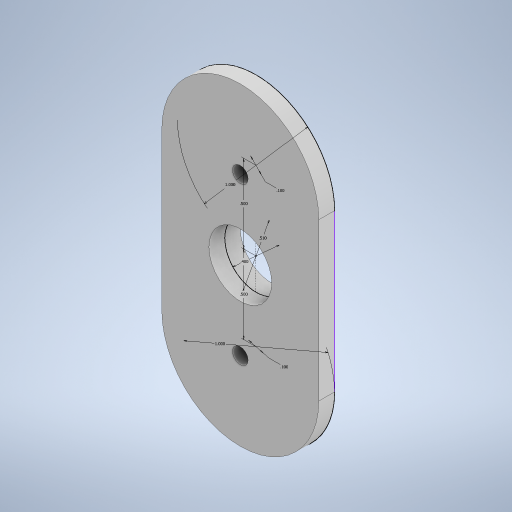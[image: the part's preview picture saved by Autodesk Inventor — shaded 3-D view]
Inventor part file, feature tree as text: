
AUTODESK INVENTOR PART (.ipt)
format: ipt  version: 2024 (Build 280153000, 153)  size: 573,952 bytes
history: native  units: in
note: dims shown in document units (in); Inventor stores cm internally (conversion verified against a paired STEP export)
features: extrude x2, sketch x1
ambient origin geometry x8: Origin, YZ Plane, XZ Plane, XY Plane, X Axis, Y Axis, Z Axis, Center Point
bodies: Solid1 (feature_tree)
feature tree (3):
  sketch  "Sketch1"  dims[d0=0.5in d1=0.5in d2=0.1in d3=0.1in d4=1.0in d5=1.0in d6=0.51in d7=0.4in d8=0.1in d9=0.0in d10=0.1in d11=0.0in]
  extrude  "Extrusion1"  Depth=0.5in
  extrude  "Extrusion2"  Depth=0.1in
